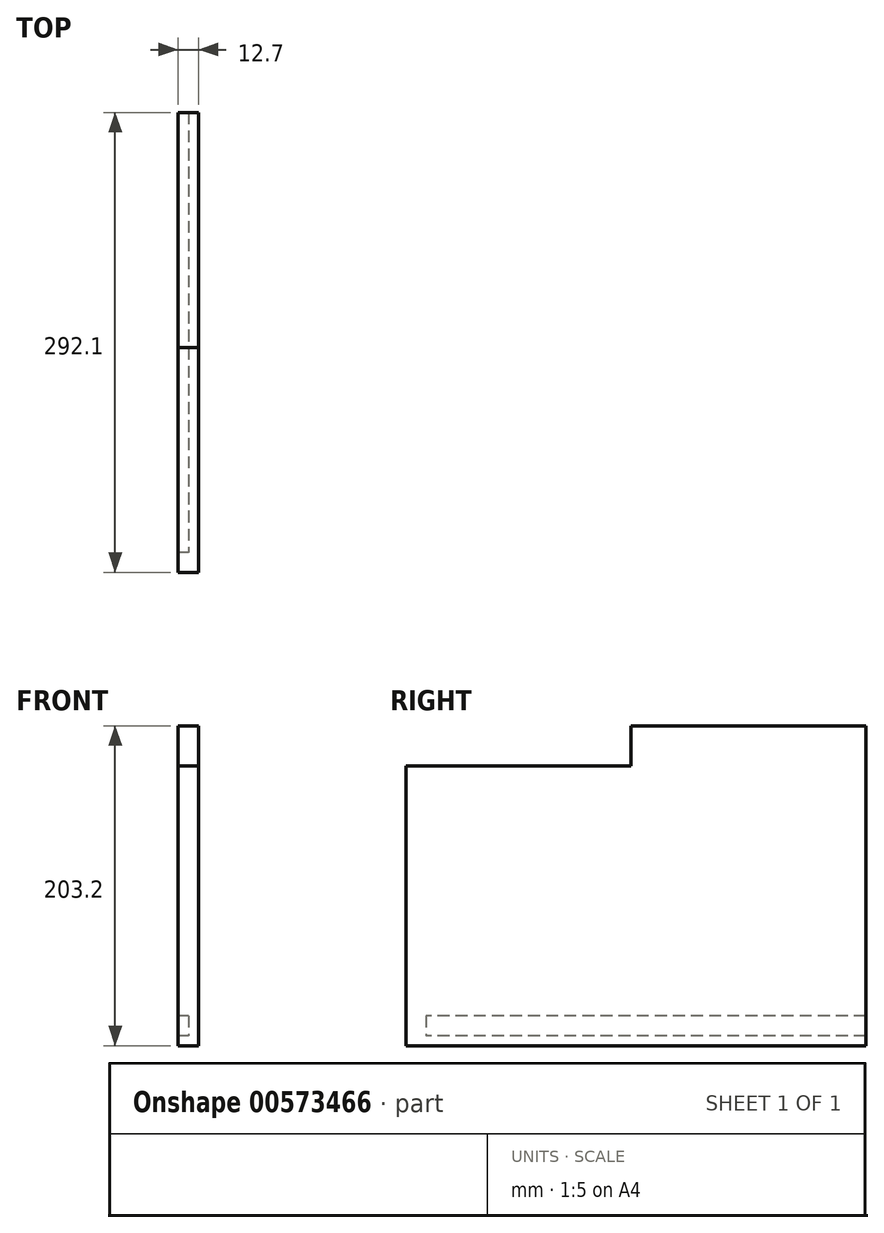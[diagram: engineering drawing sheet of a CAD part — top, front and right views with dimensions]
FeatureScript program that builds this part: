
annotation { "Feature Type Name" : "Feature", "Feature Type Description" : "" }
export const myFeature = defineFeature(function(context is Context, id is Id, definition is map)
    precondition{}
    {
        {
            var Q0;
            Q0=qCreatedBy(makeId("Right.planeOp"),FACE);
            var sketch = newSketch(context, id + "F0", { "sketchPlane" : qUnion([Q0])});
            skLineSegment(sketch, "E0.bottom", {"start": v(146.05, 88.9) * mm, "end": v(-146.05, 88.9) * mm});
            skLineSegment(sketch, "E0.top", {"start": v(146.05, -88.9) * mm, "end": v(-146.05, -88.9) * mm});
            skLineSegment(sketch, "E0.left", {"start": v(146.05, 88.9) * mm, "end": v(146.05, -88.9) * mm});
            skLineSegment(sketch, "E0.right", {"start": v(-146.05, 88.9) * mm, "end": v(-146.05, -88.9) * mm});
            skPoint(sketch, "E0.middle", {"position": v(0, 0) * mm});
            skSolve(sketch);
        }
        {
            var Q0;
            Q0=makeQuery(id+"F0.imprint","IMPRINT",FACE,{"disambiguationData":[TD([[makeQuery(id+"F0.imprint","IMPRINT",EDGE,{"derivedFrom":sQuery(id+"F0.wireOp",EDGE,"E0.bottom")}),1.0]])]});
            extrude(context, id + "F1", {"entities" : qUnion([Q0]), "depth" : 12.7 * mm, "offsetDistance" : 25.4 * mm});
        }
        {
            var Q0;
            Q0=makeQuery(id+"F1.opExtrude","CAP_FACE",FACE,{"disambiguationData":[OSD([sQuery(id+"F0.wireOp",EDGE,"E0.bottom"),sQuery(id+"F0.wireOp",EDGE,"E0.top"),sQuery(id+"F0.wireOp",EDGE,"E0.left"),sQuery(id+"F0.wireOp",EDGE,"E0.right")])],"isStart":false});
            var sketch = newSketch(context, id + "F2", { "sketchPlane" : qUnion([Q0])});
            skLineSegment(sketch, "E1.bottom", {"start": v(146.05, 88.9) * mm, "end": v(-3.18, 88.9) * mm});
            skLineSegment(sketch, "E1.top", {"start": v(146.05, 114.3) * mm, "end": v(-3.18, 114.3) * mm});
            skLineSegment(sketch, "E1.left", {"start": v(146.05, 88.9) * mm, "end": v(146.05, 114.3) * mm});
            skLineSegment(sketch, "E1.right", {"start": v(-3.18, 88.9) * mm, "end": v(-3.18, 114.3) * mm});
            skSolve(sketch);
        }
        {
            var Q0;
            Q0=makeQuery(id+"F2.imprint","IMPRINT",FACE,{"disambiguationData":[TD([[makeQuery(id+"F2.imprint","IMPRINT",EDGE,{"derivedFrom":sQuery(id+"F2.wireOp",EDGE,"E1.bottom")}),-1.0]])]});
            extrude(context, id + "F3", {"entities" : qUnion([Q0]), "operationType" : NewBodyOperationType.ADD, "oppositeDirection" : true, "depth" : 12.7 * mm, "offsetDistance" : 25.4 * mm});
        }
        {
            var Q0;
            Q0=makeQuery(id+"F3.boolean.opBoolean","MERGE",FACE,{"derivedFrom":[makeQuery(id+"F1.opExtrude","CAP_FACE",FACE,{"disambiguationData":[OSD([sQuery(id+"F0.wireOp",EDGE,"E0.bottom"),sQuery(id+"F0.wireOp",EDGE,"E0.top"),sQuery(id+"F0.wireOp",EDGE,"E0.left"),sQuery(id+"F0.wireOp",EDGE,"E0.right")])],"isStart":true}),makeQuery(id+"F3.opExtrude","CAP_FACE",FACE,{"disambiguationData":[OSD([sQuery(id+"F2.wireOp",EDGE,"E1.bottom"),sQuery(id+"F2.wireOp",EDGE,"E1.top"),sQuery(id+"F2.wireOp",EDGE,"E1.left"),sQuery(id+"F2.wireOp",EDGE,"E1.right")])],"isStart":false})]});
            var sketch = newSketch(context, id + "F4", { "sketchPlane" : qUnion([Q0])});
            skLineSegment(sketch, "E2", {"start": v(-146.05, -88.9) * mm, "end": v(-146.05, -82.55) * mm});
            skLineSegment(sketch, "E3", {"start": v(-146.05, -82.55) * mm, "end": v(-146.05, -69.85) * mm});
            skLineSegment(sketch, "E4", {"start": v(-146.05, -69.85) * mm, "end": v(133.35, -69.85) * mm});
            skLineSegment(sketch, "E5", {"start": v(133.35, -69.85) * mm, "end": v(133.35, -82.55) * mm});
            skLineSegment(sketch, "E6", {"start": v(-146.05, -82.55) * mm, "end": v(133.35, -82.55) * mm});
            skLineSegment(sketch, "E7", {"start": v(-146.05, -69.85) * mm, "end": v(-133.35, -69.85) * mm});
            skLineSegment(sketch, "E8", {"start": v(-133.35, -82.55) * mm, "end": v(-133.35, -69.85) * mm});
            skSolve(sketch);
        }
        {
            var Q0;
            Q0=makeQuery(id+"F4.imprint","IMPRINT",FACE,{"disambiguationData":[TD([[makeQuery(id+"F4.imprint","IMPRINT",EDGE,{"derivedFrom":sQuery(id+"F4.wireOp",EDGE,"E4")}),-1.0]])]});
            extrude(context, id + "F5", {"entities" : qUnion([Q0]), "operationType" : NewBodyOperationType.REMOVE, "oppositeDirection" : true, "depth" : 6.35 * mm, "offsetDistance" : 25.4 * mm});
        }
    });
